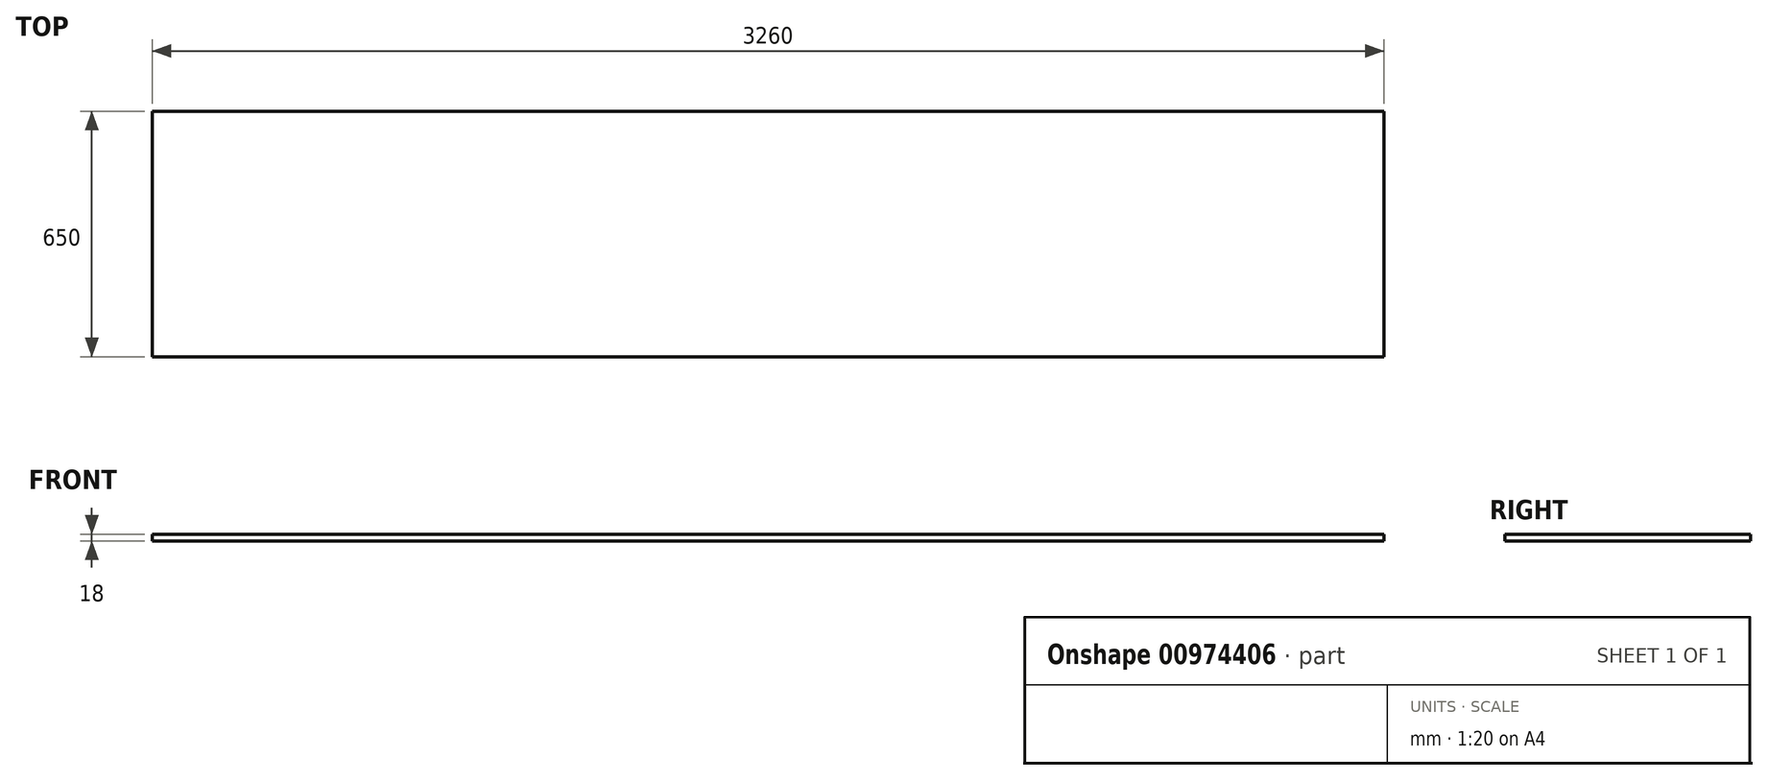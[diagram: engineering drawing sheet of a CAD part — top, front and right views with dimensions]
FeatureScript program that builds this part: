
annotation { "Feature Type Name" : "Feature", "Feature Type Description" : "" }
export const myFeature = defineFeature(function(context is Context, id is Id, definition is map)
    precondition{}
    {
        {
            var Q0;
            Q0=qCreatedBy(makeId("Top.planeOp"),FACE);
            var sketch = newSketch(context, id + "F0", { "sketchPlane" : qUnion([Q0])});
            skLineSegment(sketch, "E0.bottom", {"start": v(1630, 325) * mm, "end": v(-1630, 325) * mm});
            skLineSegment(sketch, "E0.top", {"start": v(1630, -325) * mm, "end": v(-1630, -325) * mm});
            skLineSegment(sketch, "E0.left", {"start": v(1630, 325) * mm, "end": v(1630, -325) * mm});
            skLineSegment(sketch, "E0.right", {"start": v(-1630, 325) * mm, "end": v(-1630, -325) * mm});
            skPoint(sketch, "E0.middle", {"position": v(0, 0) * mm});
            skSolve(sketch);
        }
        {
            var Q0;
            Q0=makeQuery(id+"F0.imprint","IMPRINT",FACE,{"disambiguationData":[TD([[makeQuery(id+"F0.imprint","IMPRINT",EDGE,{"derivedFrom":sQuery(id+"F0.wireOp",EDGE,"E0.bottom")}),1.0]])]});
            extrude(context, id + "F1", {"entities" : qUnion([Q0]), "depth" : 18 * mm, "offsetDistance" : 25 * mm});
        }
    });
